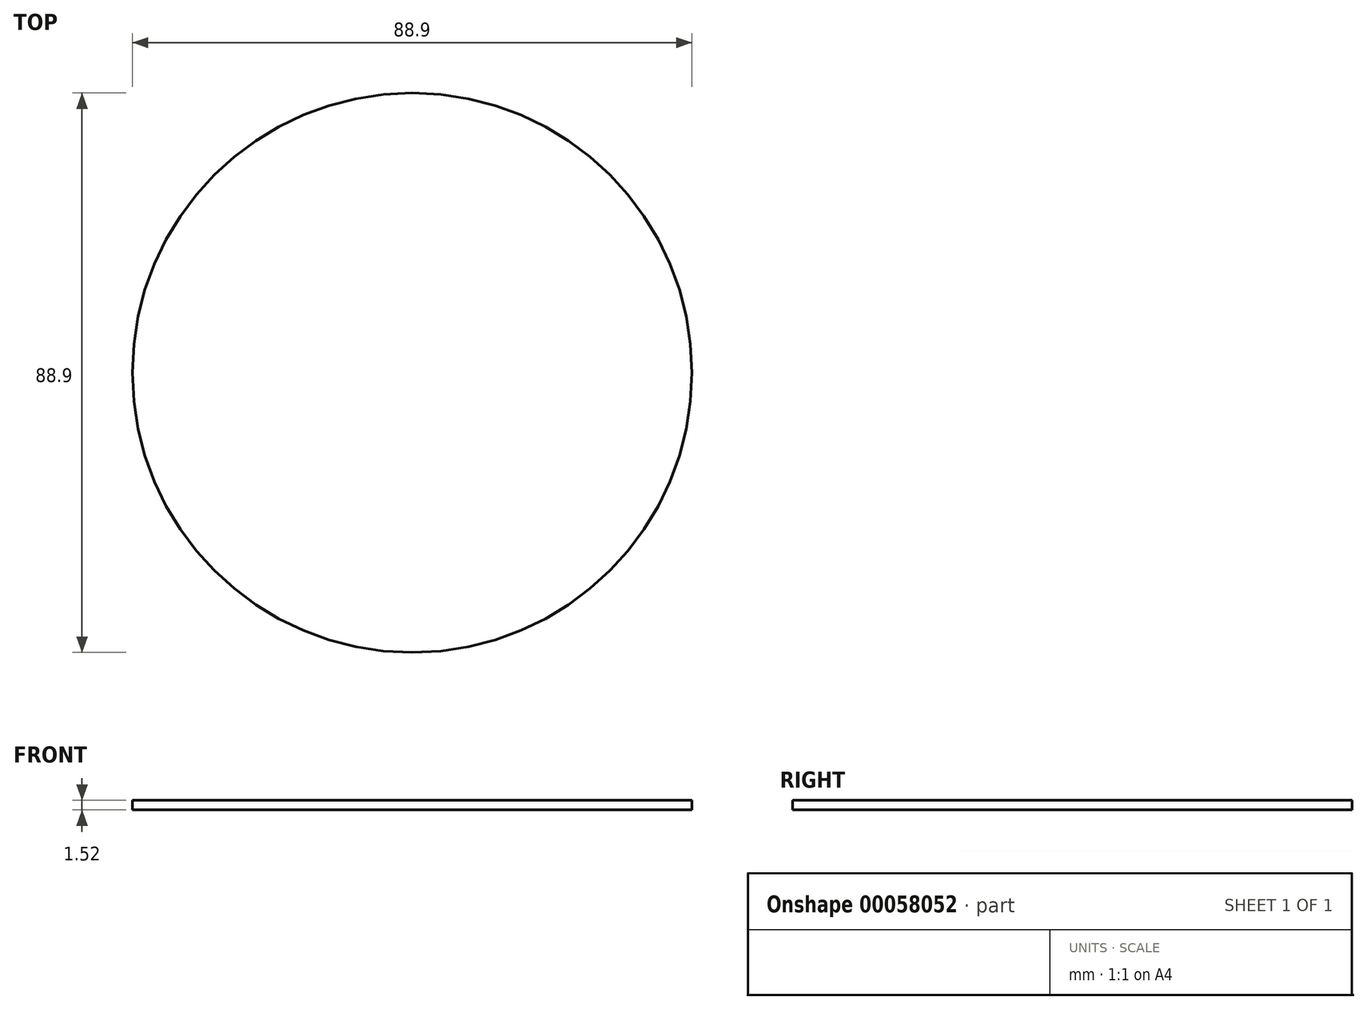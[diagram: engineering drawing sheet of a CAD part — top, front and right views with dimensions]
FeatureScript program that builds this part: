
annotation { "Feature Type Name" : "Feature", "Feature Type Description" : "" }
export const myFeature = defineFeature(function(context is Context, id is Id, definition is map)
    precondition{}
    {
        {
            var Q0;
            Q0=qCreatedBy(makeId("Top.planeOp"),FACE);
            var sketch = newSketch(context, id + "F0", { "sketchPlane" : qUnion([Q0])});
            skCircle(sketch, "E0", {"center": v(0, 0) * mm, "radius": 44.45 * mm});
            skSolve(sketch);
        }
        {
            var Q0;
            Q0 = qSketchRegion(id + "F0", true);
            extrude(context, id + "F1", {"entities" : qUnion([Q0]), "oppositeDirection" : true, "depth" : 1.52 * mm});
        }
    });
